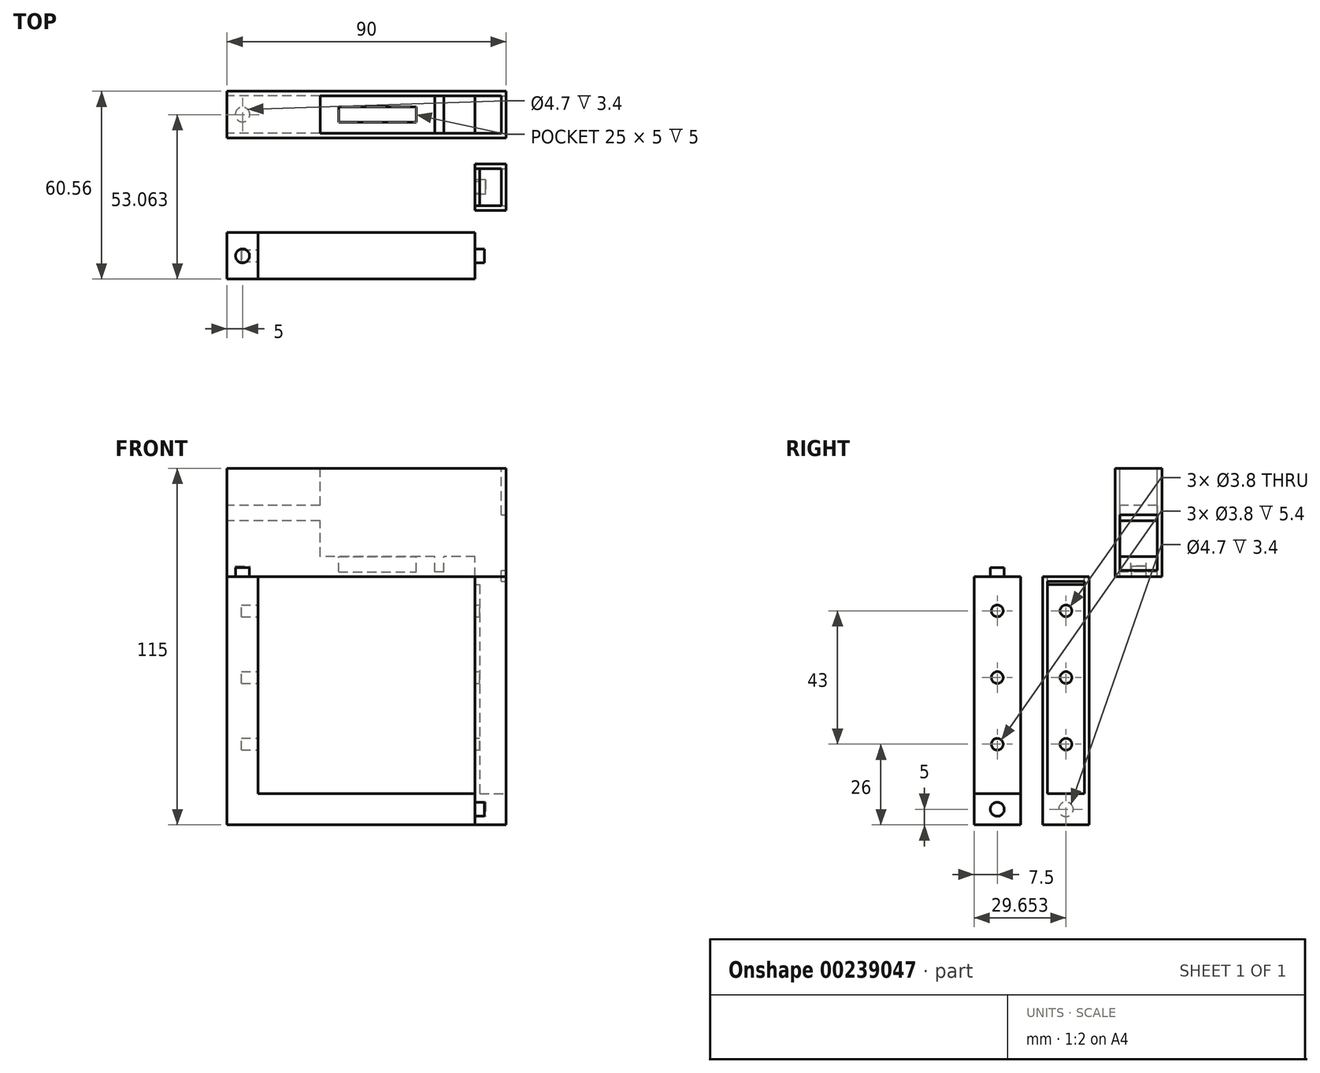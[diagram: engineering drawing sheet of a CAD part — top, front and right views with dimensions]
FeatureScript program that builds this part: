
annotation { "Feature Type Name" : "Feature", "Feature Type Description" : "" }
export const myFeature = defineFeature(function(context is Context, id is Id, definition is map)
    precondition{}
    {
        {
            var Q0;
            Q0=qCreatedBy(makeId("Front.planeOp"),FACE);
            var sketch = newSketch(context, id + "F0", { "sketchPlane" : qUnion([Q0])});
            skLineSegment(sketch, "E0", {"start": v(0, 0) * mm, "end": v(0, 80) * mm});
            skLineSegment(sketch, "E1", {"start": v(10, 80) * mm, "end": v(10, 10) * mm});
            skLineSegment(sketch, "E2", {"start": v(10, 10) * mm, "end": v(80, 10) * mm});
            skLineSegment(sketch, "E3", {"start": v(80, 10) * mm, "end": v(80, 0) * mm});
            skLineSegment(sketch, "E4", {"start": v(80, 0) * mm, "end": v(0, 0) * mm});
            skLineSegment(sketch, "E5", {"start": v(0, 80) * mm, "end": v(10, 80) * mm});
            skSolve(sketch);
        }
        {
            var Q0;
            Q0 = qSketchRegion(id + "F0", true);
            extrude(context, id + "F1", {"entities" : qUnion([Q0]), "depth" : 15 * mm});
        }
        {
            var Q0;
            Q0=makeQuery(id+"F1.opExtrude","SWEPT_FACE",FACE,{"disambiguationData":[OSD([sQuery(id+"F0.wireOp",EDGE,"E1")])]});
            var sketch = newSketch(context, id + "F2", { "sketchPlane" : qUnion([Q0])});
            skCircle(sketch, "E6", {"center": v(-7.5, 26) * mm, "radius": 1.9 * mm});
            skPoint(sketch, "E6.centerSnap0", {"position": v(-7.5, 10) * mm});
            skCircle(sketch, "E7", {"center": v(-7.5, 47.5) * mm, "radius": 1.9 * mm});
            skCircle(sketch, "E8", {"center": v(-7.5, 69) * mm, "radius": 1.9 * mm});
            skSolve(sketch);
        }
        {
            var Q0;
            Q0=makeQuery(id+"F2.imprint","IMPRINT",FACE,{"disambiguationData":[TD([[makeQuery(id+"F2.imprint","IMPRINT",EDGE,{"derivedFrom":sQuery(id+"F2.wireOp",EDGE,"E6")}),1.0]])]});
            var Q1;
            Q1=makeQuery(id+"F2.imprint","IMPRINT",FACE,{"disambiguationData":[TD([[makeQuery(id+"F2.imprint","IMPRINT",EDGE,{"derivedFrom":sQuery(id+"F2.wireOp",EDGE,"E7")}),1.0]])]});
            var Q2;
            Q2=makeQuery(id+"F2.imprint","IMPRINT",FACE,{"disambiguationData":[TD([[makeQuery(id+"F2.imprint","IMPRINT",EDGE,{"derivedFrom":sQuery(id+"F2.wireOp",EDGE,"E8")}),1.0]])]});
            extrude(context, id + "F3", {"entities" : qUnion([Q0, Q1, Q2]), "operationType" : NewBodyOperationType.REMOVE, "oppositeDirection" : true, "depth" : 5.4 * mm});
        }
        {
            var Q0;
            Q0=makeQuery(id+"F1.opExtrude","SWEPT_FACE",FACE,{"disambiguationData":[OSD([sQuery(id+"F0.wireOp",EDGE,"E3")])]});
            var sketch = newSketch(context, id + "F4", { "sketchPlane" : qUnion([Q0])});
            skCircle(sketch, "E9", {"center": v(-7.5, 5) * mm, "radius": 2.25 * mm});
            skPoint(sketch, "E9.centerSnap0", {"position": v(0, 5) * mm});
            skPoint(sketch, "E9.centerSnap1", {"position": v(-7.5, 10) * mm});
            skSolve(sketch);
        }
        {
            var Q0;
            Q0 = qSketchRegion(id + "F4", true);
            extrude(context, id + "F5", {"entities" : qUnion([Q0]), "operationType" : NewBodyOperationType.ADD, "depth" : 3 * mm});
        }
        {
            var Q0;
            Q0=makeQuery(id+"F1.opExtrude","SWEPT_FACE",FACE,{"disambiguationData":[OSD([sQuery(id+"F0.wireOp",EDGE,"E5")])]});
            var sketch = newSketch(context, id + "F6", { "sketchPlane" : qUnion([Q0])});
            skCircle(sketch, "E10", {"center": v(5, -7.5) * mm, "radius": 2.25 * mm});
            skPoint(sketch, "E10.centerSnap0", {"position": v(10, -7.5) * mm});
            skPoint(sketch, "E10.centerSnap1", {"position": v(5, 0) * mm});
            skSolve(sketch);
        }
        {
            var Q0;
            Q0 = qSketchRegion(id + "F6", true);
            extrude(context, id + "F7", {"entities" : qUnion([Q0]), "operationType" : NewBodyOperationType.ADD, "depth" : 3 * mm});
        }
        {
            var Q0;
            Q0=makeQuery(id+"F1.opExtrude","SWEPT_FACE",FACE,{"disambiguationData":[OSD([sQuery(id+"F0.wireOp",EDGE,"E5")])]});
            var sketch = newSketch(context, id + "F8", { "sketchPlane" : qUnion([Q0])});
            skLineSegment(sketch, "E11.bottom", {"start": v(0, 45.56) * mm, "end": v(90, 45.56) * mm});
            skLineSegment(sketch, "E11.top", {"start": v(0, 30.56) * mm, "end": v(90, 30.56) * mm});
            skLineSegment(sketch, "E11.left", {"start": v(0, 45.56) * mm, "end": v(0, 30.56) * mm});
            skLineSegment(sketch, "E11.right", {"start": v(90, 45.56) * mm, "end": v(90, 30.56) * mm});
            skSolve(sketch);
        }
        {
            var Q0;
            Q0 = qSketchRegion(id + "F8", true);
            extrude(context, id + "F9", {"entities" : qUnion([Q0]), "depth" : 35 * mm});
        }
        {
            var Q0;
            Q0=makeQuery(id+"F9.opExtrude","CAP_FACE",FACE,{"disambiguationData":[OSD([sQuery(id+"F8.wireOp",EDGE,"E11.bottom"),sQuery(id+"F8.wireOp",EDGE,"E11.top"),sQuery(id+"F8.wireOp",EDGE,"E11.left"),sQuery(id+"F8.wireOp",EDGE,"E11.right")])],"isStart":false});
            var sketch = newSketch(context, id + "F10", { "sketchPlane" : qUnion([Q0])});
            skLineSegment(sketch, "E12.right", {"start": v(80, 44.06) * mm, "end": v(80, 32.06) * mm});
            skLineSegment(sketch, "E13", {"start": v(80, 44.06) * mm, "end": v(88.5, 44.06) * mm});
            skLineSegment(sketch, "E14", {"start": v(88.5, 44.06) * mm, "end": v(88.5, 32.06) * mm});
            skLineSegment(sketch, "E15", {"start": v(88.5, 32.06) * mm, "end": v(80, 32.06) * mm});
            skLineSegment(sketch, "E16.bottom", {"start": v(80, 44.06) * mm, "end": v(30, 44.06) * mm});
            skLineSegment(sketch, "E16.top", {"start": v(80, 32.06) * mm, "end": v(30, 32.06) * mm});
            skLineSegment(sketch, "E16.right", {"start": v(30, 44.06) * mm, "end": v(30, 32.06) * mm});
            skLineSegment(sketch, "E17", {"start": v(70, 44.06) * mm, "end": v(70, 32.06) * mm});
            skLineSegment(sketch, "E18", {"start": v(67, 44.06) * mm, "end": v(67, 32.06) * mm});
            skSolve(sketch);
        }
        {
            var Q0;
            Q0=makeQuery(id+"F9.opExtrude","CAP_FACE",FACE,{"disambiguationData":[OSD([sQuery(id+"F8.wireOp",EDGE,"E11.bottom"),sQuery(id+"F8.wireOp",EDGE,"E11.top"),sQuery(id+"F8.wireOp",EDGE,"E11.left"),sQuery(id+"F8.wireOp",EDGE,"E11.right")])],"isStart":true});
            var sketch = newSketch(context, id + "F11", { "sketchPlane" : qUnion([Q0])});
            skCircle(sketch, "E19", {"center": v(5, -38.06) * mm, "radius": 2.35 * mm});
            skPoint(sketch, "E19.centerSnap0", {"position": v(0, -38.06) * mm});
            skSolve(sketch);
        }
        {
            var Q0;
            Q0 = qSketchRegion(id + "F11", true);
            extrude(context, id + "F12", {"entities" : qUnion([Q0]), "operationType" : NewBodyOperationType.REMOVE, "oppositeDirection" : true, "depth" : 3.4 * mm});
        }
        {
            var Q0;
            Q0=makeQuery(id+"F10.imprint","IMPRINT",FACE,{"disambiguationData":[TD([[makeQuery(id+"F10.imprint","IMPRINT",EDGE,{"derivedFrom":sQuery(id+"F10.wireOp",EDGE,"E13")}),-1.0]])]});
            extrude(context, id + "F13", {"entities" : qUnion([Q0]), "operationType" : NewBodyOperationType.REMOVE, "endBound" : BoundingType.THROUGH_ALL, "oppositeDirection" : true, "depth" : 25 * mm});
        }
        {
            var Q0;
            {var subQ0=sQuery(id+"F10.wireOp",EDGE,"E12.right");Q0=makeQuery(id+"F10.imprint","IMPRINT",FACE,{"disambiguationData":[TD([[makeQuery(id+"F10.imprint","IMPRINT",EDGE,{"derivedFrom":subQ0}),-1.0]])]});}
            var Q1;
            {var subQ0=sQuery(id+"F10.wireOp",EDGE,"E16.right");Q1=makeQuery(id+"F10.imprint","IMPRINT",FACE,{"disambiguationData":[TD([[makeQuery(id+"F10.imprint","IMPRINT",EDGE,{"derivedFrom":subQ0}),1.0]])]});}
            extrude(context, id + "F14", {"entities" : qUnion([Q0, Q1]), "operationType" : NewBodyOperationType.REMOVE, "oppositeDirection" : true, "depth" : 28.5 * mm});
        }
        {
            var Q0;
            {var subQ0=sQuery(id+"F10.wireOp",EDGE,"E17");Q0=makeQuery(id+"F10.imprint","IMPRINT",FACE,{"disambiguationData":[TD([[makeQuery(id+"F10.imprint","IMPRINT",EDGE,{"derivedFrom":subQ0}),-1.0]])]});}
            extrude(context, id + "F15", {"entities" : qUnion([Q0]), "operationType" : NewBodyOperationType.REMOVE, "oppositeDirection" : true, "depth" : 33.5 * mm});
        }
        {
            var Q0;
            Q0=makeQuery(id+"F1.opExtrude","SWEPT_FACE",FACE,{"disambiguationData":[OSD([sQuery(id+"F0.wireOp",EDGE,"E3")])]});
            var sketch = newSketch(context, id + "F16", { "sketchPlane" : qUnion([Q0])});
            skLineSegment(sketch, "E20.bottom", {"start": v(7.15, 0) * mm, "end": v(22.15, 0) * mm});
            skLineSegment(sketch, "E20.top", {"start": v(7.15, 80) * mm, "end": v(22.15, 80) * mm});
            skLineSegment(sketch, "E20.left", {"start": v(7.15, 0) * mm, "end": v(7.15, 80) * mm});
            skLineSegment(sketch, "E20.right", {"start": v(22.15, 0) * mm, "end": v(22.15, 80) * mm});
            skSolve(sketch);
        }
        {
            var Q0;
            Q0=makeQuery(id+"F16.imprint","IMPRINT",FACE,{"disambiguationData":[TD([[makeQuery(id+"F16.imprint","IMPRINT",EDGE,{"derivedFrom":sQuery(id+"F16.wireOp",EDGE,"E20.bottom")}),1.0]])]});
            extrude(context, id + "F17", {"entities" : qUnion([Q0]), "depth" : 10 * mm});
        }
        {
            var Q0;
            Q0=makeQuery(id+"F17.opExtrude","CAP_FACE",FACE,{"disambiguationData":[OSD([sQuery(id+"F16.wireOp",EDGE,"E20.bottom"),sQuery(id+"F16.wireOp",EDGE,"E20.top"),sQuery(id+"F16.wireOp",EDGE,"E20.left"),sQuery(id+"F16.wireOp",EDGE,"E20.right")])],"isStart":false});
            var sketch = newSketch(context, id + "F18", { "sketchPlane" : qUnion([Q0])});
            skLineSegment(sketch, "E21.bottom", {"start": v(8.65, 78.5) * mm, "end": v(20.65, 78.5) * mm});
            skLineSegment(sketch, "E21.top", {"start": v(8.65, 10) * mm, "end": v(20.65, 10) * mm});
            skLineSegment(sketch, "E21.left", {"start": v(8.65, 78.5) * mm, "end": v(8.65, 10) * mm});
            skLineSegment(sketch, "E21.right", {"start": v(20.65, 78.5) * mm, "end": v(20.65, 10) * mm});
            skSolve(sketch);
        }
        {
            var Q0;
            Q0=makeQuery(id+"F18.imprint","IMPRINT",FACE,{"disambiguationData":[TD([[makeQuery(id+"F18.imprint","IMPRINT",EDGE,{"derivedFrom":sQuery(id+"F18.wireOp",EDGE,"E21.bottom")}),-1.0]])]});
            extrude(context, id + "F19", {"entities" : qUnion([Q0]), "operationType" : NewBodyOperationType.REMOVE, "oppositeDirection" : true, "depth" : 8.5 * mm});
        }
        {
            var Q0;
            Q0=makeQuery(id+"F17.opExtrude","SWEPT_FACE",FACE,{"disambiguationData":[OSD([sQuery(id+"F16.wireOp",EDGE,"E20.top")])]});
            var sketch = newSketch(context, id + "F20", { "sketchPlane" : qUnion([Q0])});
            skLineSegment(sketch, "E22.bottom", {"start": v(80, 20.65) * mm, "end": v(88.5, 20.65) * mm});
            skLineSegment(sketch, "E22.top", {"start": v(80, 8.65) * mm, "end": v(88.5, 8.65) * mm});
            skLineSegment(sketch, "E22.left", {"start": v(80, 20.65) * mm, "end": v(80, 8.65) * mm});
            skLineSegment(sketch, "E22.right", {"start": v(88.5, 20.65) * mm, "end": v(88.5, 8.65) * mm});
            skSolve(sketch);
        }
        {
            var Q0;
            Q0=makeQuery(id+"F20.imprint","IMPRINT",FACE,{"disambiguationData":[TD([[makeQuery(id+"F20.imprint","IMPRINT",EDGE,{"derivedFrom":sQuery(id+"F20.wireOp",EDGE,"E22.bottom")}),-1.0]])]});
            extrude(context, id + "F21", {"entities" : qUnion([Q0]), "operationType" : NewBodyOperationType.REMOVE, "oppositeDirection" : true, "depth" : 2.5 * mm});
        }
        {
            var Q0;
            Q0=makeQuery(id+"F19.boolean.opBoolean","COPY",FACE,{"derivedFrom":makeQuery(id+"F19.opExtrude","CAP_FACE",FACE,{"disambiguationData":[OSD([sQuery(id+"F18.wireOp",EDGE,"E21.bottom"),sQuery(id+"F18.wireOp",EDGE,"E21.top"),sQuery(id+"F18.wireOp",EDGE,"E21.left"),sQuery(id+"F18.wireOp",EDGE,"E21.right")])],"isStart":false})});
            var sketch = newSketch(context, id + "F22", { "sketchPlane" : qUnion([Q0])});
            skCircle(sketch, "E23", {"center": v(14.65, 26) * mm, "radius": 1.9 * mm});
            skPoint(sketch, "E23.centerSnap0", {"position": v(14.65, 10) * mm});
            skCircle(sketch, "E24", {"center": v(14.65, 47.5) * mm, "radius": 1.9 * mm});
            skCircle(sketch, "E25", {"center": v(14.65, 69) * mm, "radius": 1.9 * mm});
            skSolve(sketch);
        }
        {
            var Q0;
            Q0=makeQuery(id+"F22.imprint","IMPRINT",FACE,{"disambiguationData":[TD([[makeQuery(id+"F22.imprint","IMPRINT",EDGE,{"derivedFrom":sQuery(id+"F22.wireOp",EDGE,"E25")}),1.0]])]});
            var Q1;
            Q1=makeQuery(id+"F22.imprint","IMPRINT",FACE,{"disambiguationData":[TD([[makeQuery(id+"F22.imprint","IMPRINT",EDGE,{"derivedFrom":sQuery(id+"F22.wireOp",EDGE,"E24")}),1.0]])]});
            var Q2;
            Q2=makeQuery(id+"F22.imprint","IMPRINT",FACE,{"disambiguationData":[TD([[makeQuery(id+"F22.imprint","IMPRINT",EDGE,{"derivedFrom":sQuery(id+"F22.wireOp",EDGE,"E23")}),1.0]])]});
            extrude(context, id + "F23", {"entities" : qUnion([Q0, Q1, Q2]), "operationType" : NewBodyOperationType.REMOVE, "endBound" : BoundingType.THROUGH_ALL, "oppositeDirection" : true, "depth" : 25 * mm});
        }
        {
            var Q0;
            Q0=makeQuery(id+"F17.opExtrude","CAP_FACE",FACE,{"disambiguationData":[OSD([sQuery(id+"F16.wireOp",EDGE,"E20.bottom"),sQuery(id+"F16.wireOp",EDGE,"E20.top"),sQuery(id+"F16.wireOp",EDGE,"E20.left"),sQuery(id+"F16.wireOp",EDGE,"E20.right")])],"isStart":true});
            var sketch = newSketch(context, id + "F24", { "sketchPlane" : qUnion([Q0])});
            skCircle(sketch, "E26", {"center": v(-14.65, 5) * mm, "radius": 2.35 * mm});
            skPoint(sketch, "E26.centerSnap0", {"position": v(-14.65, 0) * mm});
            skSolve(sketch);
        }
        {
            var Q0;
            Q0=makeQuery(id+"F24.imprint","IMPRINT",FACE,{"disambiguationData":[TD([[makeQuery(id+"F24.imprint","IMPRINT",EDGE,{"derivedFrom":sQuery(id+"F24.wireOp",EDGE,"E26")}),1.0]])]});
            extrude(context, id + "F25", {"entities" : qUnion([Q0]), "operationType" : NewBodyOperationType.REMOVE, "oppositeDirection" : true, "depth" : 3.4 * mm});
        }
        {
            var Q0;
            Q0=makeQuery(id+"F14.boolean.opBoolean","COPY",FACE,{"derivedFrom":makeQuery(id+"F14.opExtrude","CAP_FACE",FACE,{"disambiguationData":[OSD([sQuery(id+"F10.wireOp",EDGE,"E16.bottom"),sQuery(id+"F10.wireOp",EDGE,"E16.top"),sQuery(id+"F10.wireOp",EDGE,"E16.right"),sQuery(id+"F10.wireOp",EDGE,"E18")])],"isStart":false})});
            var sketch = newSketch(context, id + "F26", { "sketchPlane" : qUnion([Q0])});
            skLineSegment(sketch, "E27.bottom", {"start": v(36, 40.56) * mm, "end": v(61, 40.56) * mm});
            skLineSegment(sketch, "E27.top", {"start": v(36, 35.56) * mm, "end": v(61, 35.56) * mm});
            skLineSegment(sketch, "E27.left", {"start": v(36, 40.56) * mm, "end": v(36, 35.56) * mm});
            skLineSegment(sketch, "E27.right", {"start": v(61, 40.56) * mm, "end": v(61, 35.56) * mm});
            skSolve(sketch);
        }
        {
            var Q0;
            Q0=makeQuery(id+"F26.imprint","IMPRINT",FACE,{"disambiguationData":[TD([[makeQuery(id+"F26.imprint","IMPRINT",EDGE,{"derivedFrom":sQuery(id+"F26.wireOp",EDGE,"E27.bottom")}),-1.0]])]});
            extrude(context, id + "F27", {"entities" : qUnion([Q0]), "operationType" : NewBodyOperationType.REMOVE, "oppositeDirection" : true, "depth" : 5 * mm});
        }
        {
            var Q0;
            Q0=makeQuery(id+"F9.opExtrude","SWEPT_FACE",FACE,{"disambiguationData":[OSD([sQuery(id+"F8.wireOp",EDGE,"E11.left")])]});
            var sketch = newSketch(context, id + "F28", { "sketchPlane" : qUnion([Q0])});
            skLineSegment(sketch, "E28.bottom", {"start": v(-44.06, 103) * mm, "end": v(-32.06, 103) * mm});
            skLineSegment(sketch, "E28.top", {"start": v(-44.06, 98) * mm, "end": v(-32.06, 98) * mm});
            skLineSegment(sketch, "E28.left", {"start": v(-44.06, 103) * mm, "end": v(-44.06, 98) * mm});
            skLineSegment(sketch, "E28.right", {"start": v(-32.06, 103) * mm, "end": v(-32.06, 98) * mm});
            skSolve(sketch);
        }
        {
            var Q0;
            Q0 = qSketchRegion(id + "F28", true);
            extrude(context, id + "F29", {"entities" : qUnion([Q0]), "operationType" : NewBodyOperationType.REMOVE, "oppositeDirection" : true, "depth" : 50 * mm});
        }
        {
            var Q0;
            Q0=makeQuery(id+"F9.opExtrude","SWEPT_FACE",FACE,{"disambiguationData":[OSD([sQuery(id+"F8.wireOp",EDGE,"E11.right")])]});
            var sketch = newSketch(context, id + "F30", { "sketchPlane" : qUnion([Q0])});
            skLineSegment(sketch, "E29.bottom", {"start": v(32.06, 82) * mm, "end": v(44.06, 82) * mm});
            skLineSegment(sketch, "E29.top", {"start": v(32.06, 100) * mm, "end": v(44.06, 100) * mm});
            skLineSegment(sketch, "E29.left", {"start": v(32.06, 82) * mm, "end": v(32.06, 100) * mm});
            skLineSegment(sketch, "E29.right", {"start": v(44.06, 82) * mm, "end": v(44.06, 100) * mm});
            skSolve(sketch);
        }
        {
            var Q0;
            Q0 = qSketchRegion(id + "F30", true);
            extrude(context, id + "F31", {"entities" : qUnion([Q0]), "operationType" : NewBodyOperationType.REMOVE, "oppositeDirection" : true, "depth" : 2 * mm});
        }
    });
